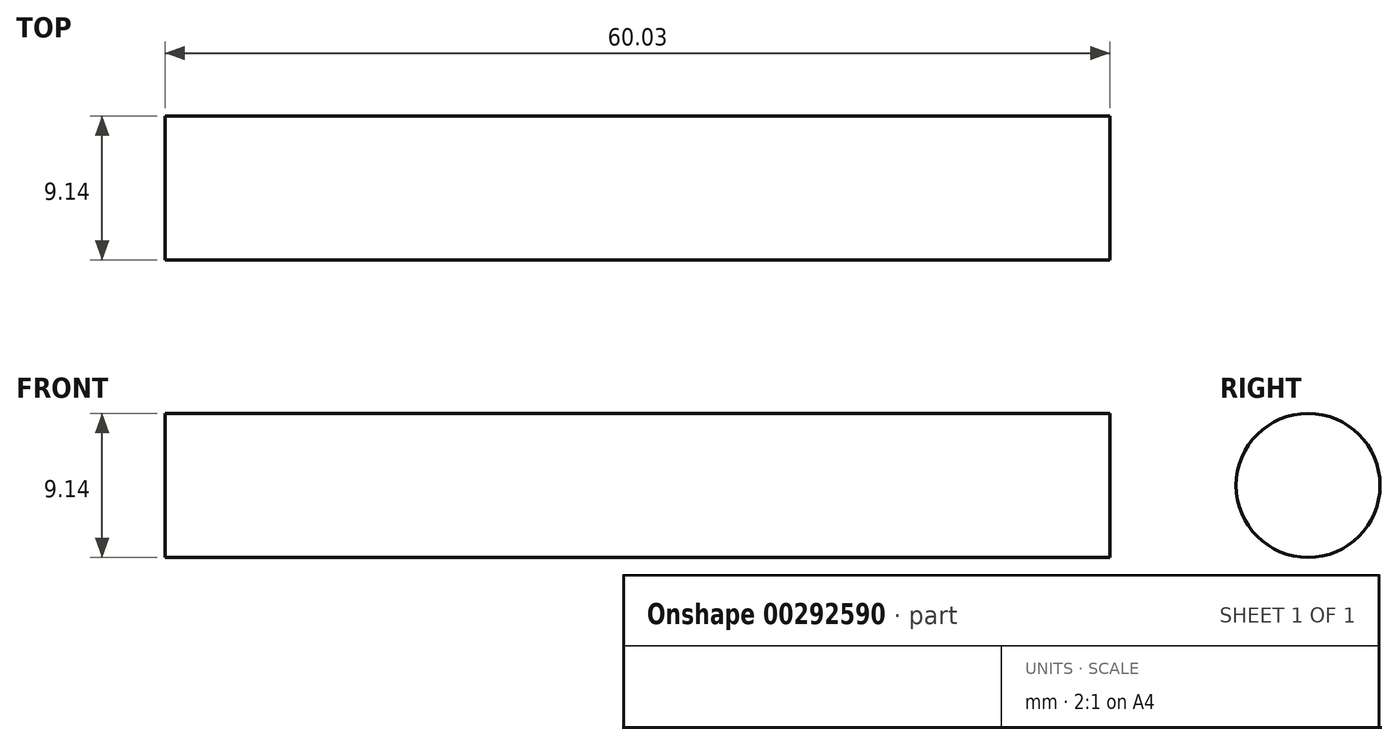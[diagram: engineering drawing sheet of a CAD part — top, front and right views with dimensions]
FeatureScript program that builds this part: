
annotation { "Feature Type Name" : "Feature", "Feature Type Description" : "" }
export const myFeature = defineFeature(function(context is Context, id is Id, definition is map)
    precondition{}
    {
        {
            var Q0;
            Q0=qCreatedBy(makeId("Top.planeOp"),FACE);
            var sketch = newSketch(context, id + "F0", { "sketchPlane" : qUnion([Q0])});
            skArc(sketch, "E0", {"start": v(4.24, -6.24) * mm, "mid": v(34.7, 0.67) * mm, "end": v(3.77, 4.99) * mm});
            skLineSegment(sketch, "E1", {"start": v(-60.03, 0) * mm, "end": v(0, 0) * mm});
            skArc(sketch, "E2", {"start": v(0, 0) * mm, "mid": v(2.3, 2.18) * mm, "end": v(3.77, 4.99) * mm});
            skSolve(sketch);
        }
        {
            var Q0;
            Q0=qCreatedBy(makeId("Right.planeOp"),FACE);
            var sketch = newSketch(context, id + "F1", { "sketchPlane" : qUnion([Q0])});
            skCircle(sketch, "E3", {"center": v(0, 0) * mm, "radius": 4.57 * mm});
            skSolve(sketch);
        }
        {
            var Q0;
            Q0 = qSketchRegion(id + "F1", true);
            var Q1;
            Q1 = qSketchRegion(id + "F0", true);
            var Q2;
            Q2=sQuery(id+"F0.wireOp",EDGE,"E1");
            sweep(context, id + "F2", {"profiles" : qUnion([Q0, Q1]), "path" : qUnion([Q2])});
        }
    });
